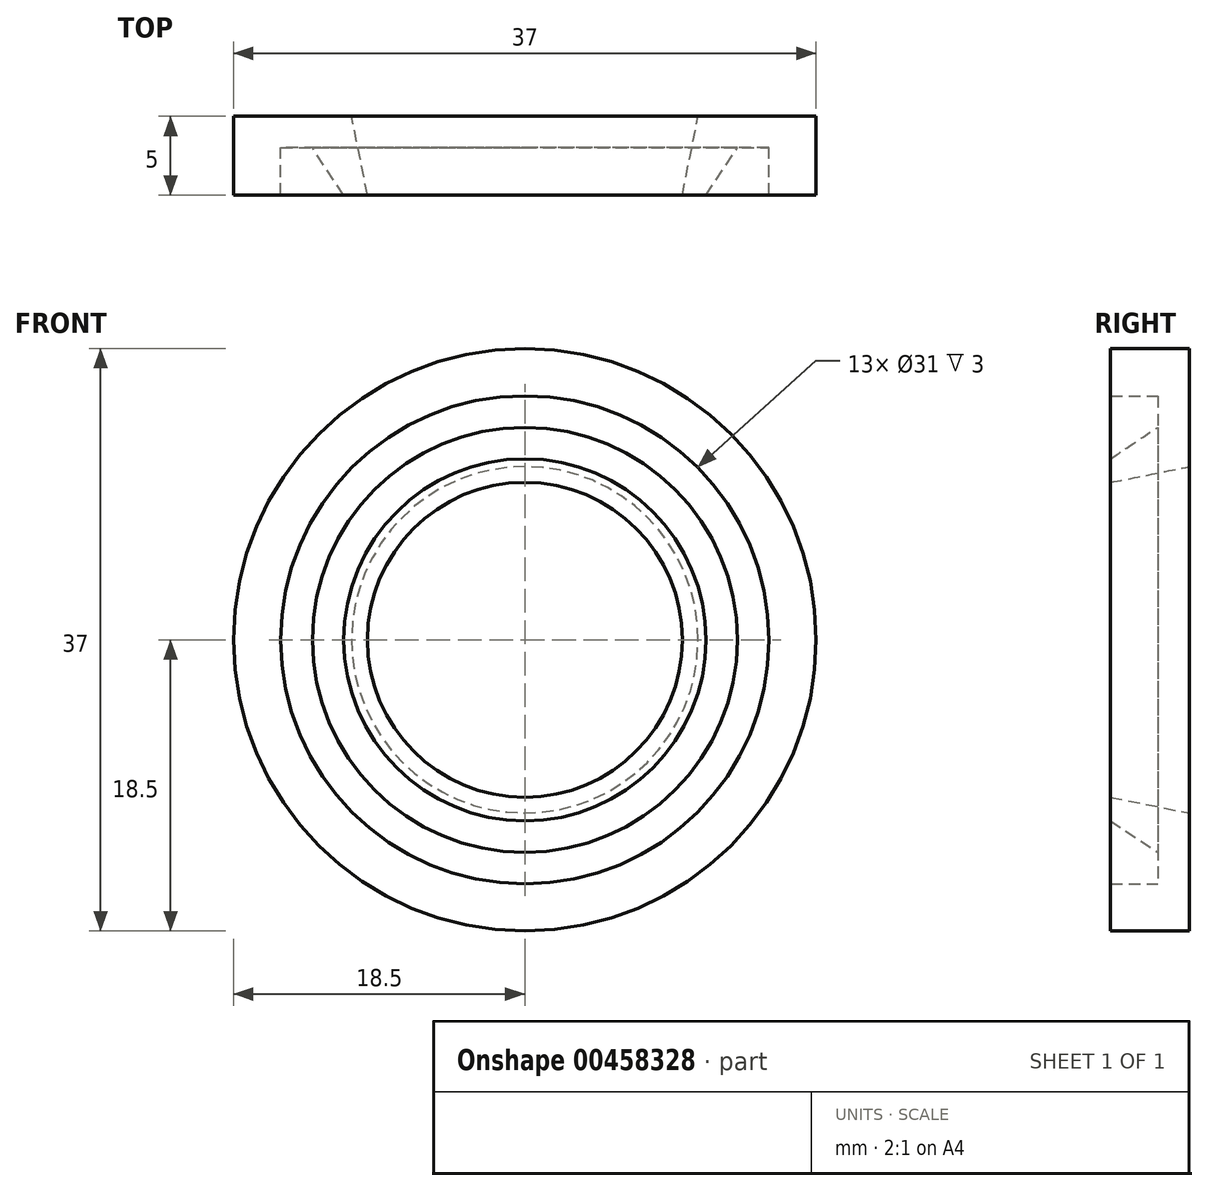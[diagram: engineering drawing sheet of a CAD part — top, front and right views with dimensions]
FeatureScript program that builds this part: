
annotation { "Feature Type Name" : "Feature", "Feature Type Description" : "" }
export const myFeature = defineFeature(function(context is Context, id is Id, definition is map)
    precondition{}
    {
        {
            var Q0;
            Q0=qCreatedBy(makeId("Right.planeOp"),FACE);
            var sketch = newSketch(context, id + "F0", { "sketchPlane" : qUnion([Q0])});
            skLineSegment(sketch, "E0", {"start": v(0, 0) * mm, "end": v(-18.29, 0) * mm, "construction": true});
            skLineSegment(sketch, "E1", {"start": v(0, 0) * mm, "end": v(0, 11) * mm, "construction": true});
            skLineSegment(sketch, "E2", {"start": v(3.67, 0) * mm, "end": v(3.67, 13) * mm, "construction": true});
            skPoint(sketch, "E2.startSnap0", {"position": v(-9.14, 0) * mm});
            skLineSegment(sketch, "E3", {"start": v(8.49, 0) * mm, "end": v(8.49, 18.5) * mm, "construction": true});
            skLineSegment(sketch, "E4", {"start": v(-5, 0) * mm, "end": v(-5, 10) * mm, "construction": true});
            skLineSegment(sketch, "E5", {"start": v(0, 11) * mm, "end": v(0, 18.5) * mm});
            skLineSegment(sketch, "E6", {"start": v(0, 18.5) * mm, "end": v(-5, 18.5) * mm});
            skLineSegment(sketch, "E7", {"start": v(-5, 18.5) * mm, "end": v(-5, 15.5) * mm});
            skLineSegment(sketch, "E8", {"start": v(-5, 15.5) * mm, "end": v(-2, 15.5) * mm});
            skLineSegment(sketch, "E9", {"start": v(-2, 15.5) * mm, "end": v(-2, 13.5) * mm});
            skLineSegment(sketch, "E10", {"start": v(0, 11) * mm, "end": v(-5, 10) * mm});
            skLineSegment(sketch, "E11", {"start": v(-5, 10) * mm, "end": v(-5, 11.5) * mm});
            skLineSegment(sketch, "E12", {"start": v(-5, 11.5) * mm, "end": v(-2, 13.5) * mm});
            skSolve(sketch);
        }
        {
            var Q0;
            Q0=makeQuery(id+"F0.imprint","IMPRINT",FACE,{"disambiguationData":[TD([[makeQuery(id+"F0.imprint","IMPRINT",EDGE,{"derivedFrom":sQuery(id+"F0.wireOp",EDGE,"E5")}),1.0]])]});
            var Q1;
            Q1=sQuery(id+"F0.wireOp",EDGE,"E0");
            revolve(context, id + "F1", {"entities" : qUnion([Q0]), "axis" : qUnion([Q1]), "revolveType" : RevolveType.FULL});
        }
    });
